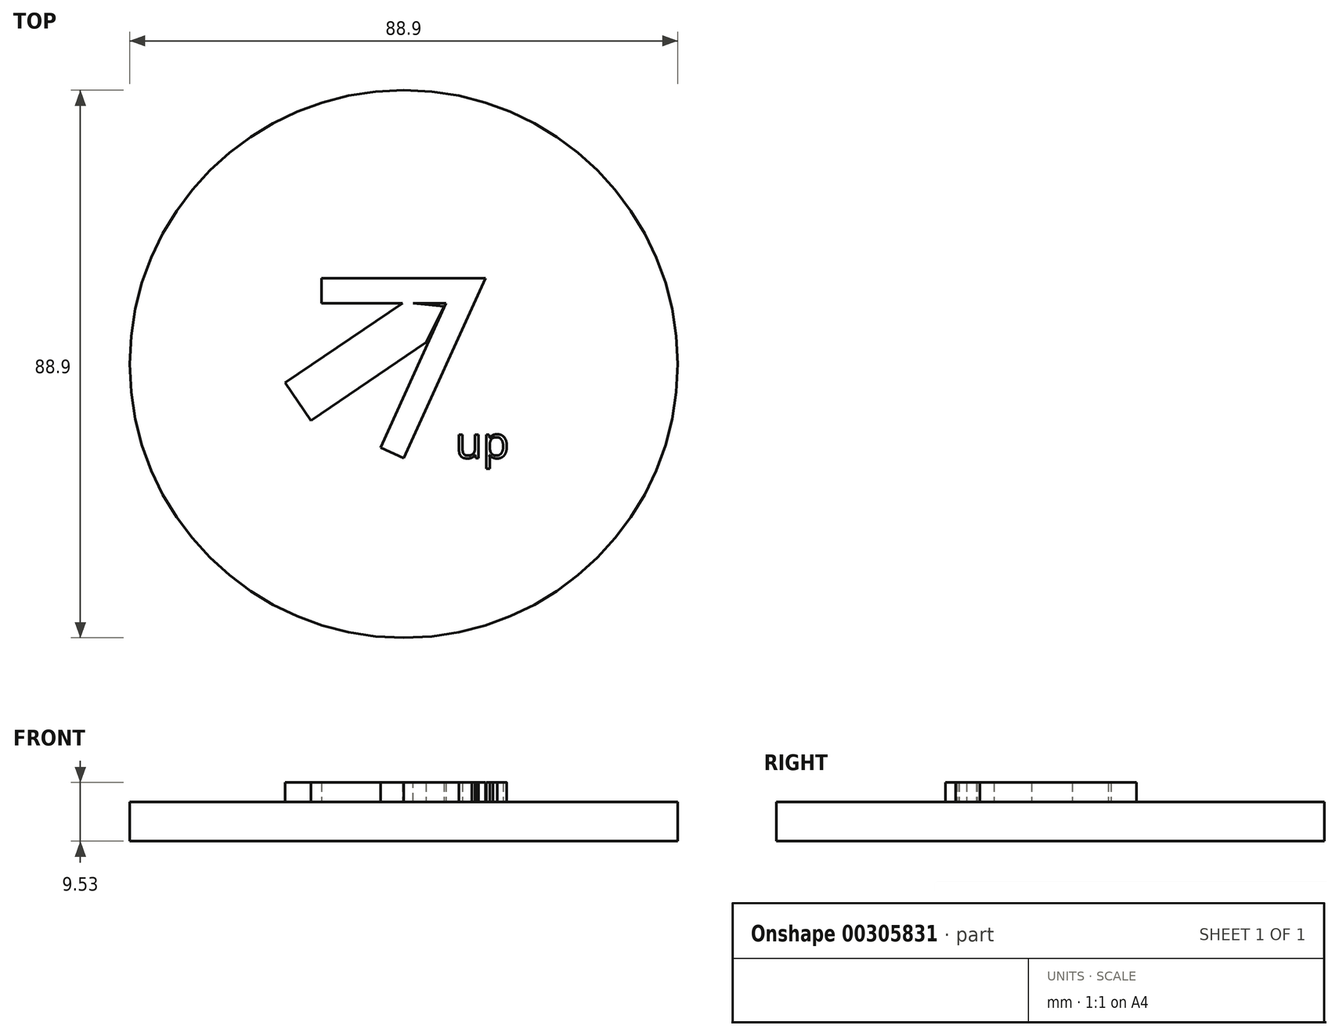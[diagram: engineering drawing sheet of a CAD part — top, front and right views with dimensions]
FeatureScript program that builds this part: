
annotation { "Feature Type Name" : "Feature", "Feature Type Description" : "" }
export const myFeature = defineFeature(function(context is Context, id is Id, definition is map)
    precondition{}
    {
        {
            var Q0;
            Q0=qCreatedBy(makeId("Top.planeOp"),FACE);
            var sketch = newSketch(context, id + "F0", { "sketchPlane" : qUnion([Q0])});
            skCircle(sketch, "E0", {"center": v(0, 0) * mm, "radius": 44.45 * mm});
            skSolve(sketch);
        }
        {
            var Q0;
            Q0 = qSketchRegion(id + "F0", true);
            extrude(context, id + "F1", {"entities" : qUnion([Q0]), "depth" : 6.35 * mm});
        }
        {
            var Q0;
            Q0=makeQuery(id+"F1.opExtrude","CAP_FACE",FACE,{"disambiguationData":[OSD([sQuery(id+"F0.wireOp",EDGE,"E0")])],"isStart":false});
            var sketch = newSketch(context, id + "F2", { "sketchPlane" : qUnion([Q0])});
            skLineSegment(sketch, "E1", {"start": v(-13.33, 13.95) * mm, "end": v(13.28, 13.95) * mm});
            skLineSegment(sketch, "E2", {"start": v(13.28, 13.95) * mm, "end": v(0, -15.28) * mm});
            skLineSegment(sketch, "E3", {"start": v(0, -15.28) * mm, "end": v(-3.75, -13.57) * mm});
            skLineSegment(sketch, "E4", {"start": v(-3.75, -13.57) * mm, "end": v(6.88, 9.84) * mm});
            skLineSegment(sketch, "E5", {"start": v(6.88, 9.84) * mm, "end": v(-13.33, 9.84) * mm});
            skLineSegment(sketch, "E6", {"start": v(-13.33, 9.84) * mm, "end": v(-13.33, 13.95) * mm});
            skSolve(sketch);
        }
        {
            var Q0;
            Q0=makeQuery(id+"F2.imprint","IMPRINT",FACE,{"disambiguationData":[TD([[makeQuery(id+"F2.imprint","IMPRINT",EDGE,{"derivedFrom":sQuery(id+"F2.wireOp",EDGE,"E1")}),1.0]])]});
            var sketch = newSketch(context, id + "F3", { "sketchPlane" : qUnion([Q0])});
            skLineSegment(sketch, "E7", {"start": v(-19.22, -3.06) * mm, "end": v(-15.08, -9.17) * mm});
            skLineSegment(sketch, "E8", {"start": v(-15.08, -9.17) * mm, "end": v(3.64, 3.53) * mm});
            skLineSegment(sketch, "E9", {"start": v(3.64, 3.53) * mm, "end": v(6.52, 9.37) * mm});
            skLineSegment(sketch, "E10", {"start": v(-19.22, -3.06) * mm, "end": v(0, 9.98) * mm});
            skLineSegment(sketch, "E11", {"start": v(0, 9.98) * mm, "end": v(6.52, 9.37) * mm});
            skSolve(sketch);
        }
        {
            var Q0;
            Q0 = qSketchRegion(id + "F2", true);
            var Q1;
            Q1 = qSketchRegion(id + "F3", true);
            extrude(context, id + "F4", {"entities" : qUnion([Q0, Q1]), "operationType" : NewBodyOperationType.ADD, "depth" : 3.17 * mm});
        }
        {
            var Q0;
            Q0=makeQuery(id+"F1.opExtrude","CAP_FACE",FACE,{"disambiguationData":[OSD([sQuery(id+"F0.wireOp",EDGE,"E0")])],"isStart":false});
            var sketch = newSketch(context, id + "F5", { "sketchPlane" : qUnion([Q0])});
            skLineSegment(sketch, "E12", {"start": v(-0.2, 9.84) * mm, "end": v(1.52, 9.84) * mm});
            skSolve(sketch);
        }
        {
            var Q0;
            Q0=sQuery(id+"F5.wireOp",EDGE,"E12");
            extrude(context, id + "F6", {"bodyType" : ToolBodyType.SURFACE, "surfaceEntities" : qUnion([Q0]), "depth" : 3.17 * mm});
        }
        {
            var Q0;
            Q0=makeQuery(id+"F1.opExtrude","CAP_FACE",FACE,{"disambiguationData":[OSD([sQuery(id+"F0.wireOp",EDGE,"E0")])],"isStart":false});
            var sketch = newSketch(context, id + "F7", { "sketchPlane" : qUnion([Q0])});
            skText(sketch, "E13", { "text": "up\n", "fontName": "OpenSans-Regular.ttf"});
            const initialGuessF7  = {"E13": [0.0084, -0.01528, 1, 0, 0.00512]};
            skSetInitialGuess(sketch, initialGuessF7);
            skSolve(sketch);
        }
        {
            var Q0;
            Q0 = qSketchRegion(id + "F7", true);
            extrude(context, id + "F8", {"entities" : qUnion([Q0]), "operationType" : NewBodyOperationType.ADD, "depth" : 3.17 * mm});
        }
    });
